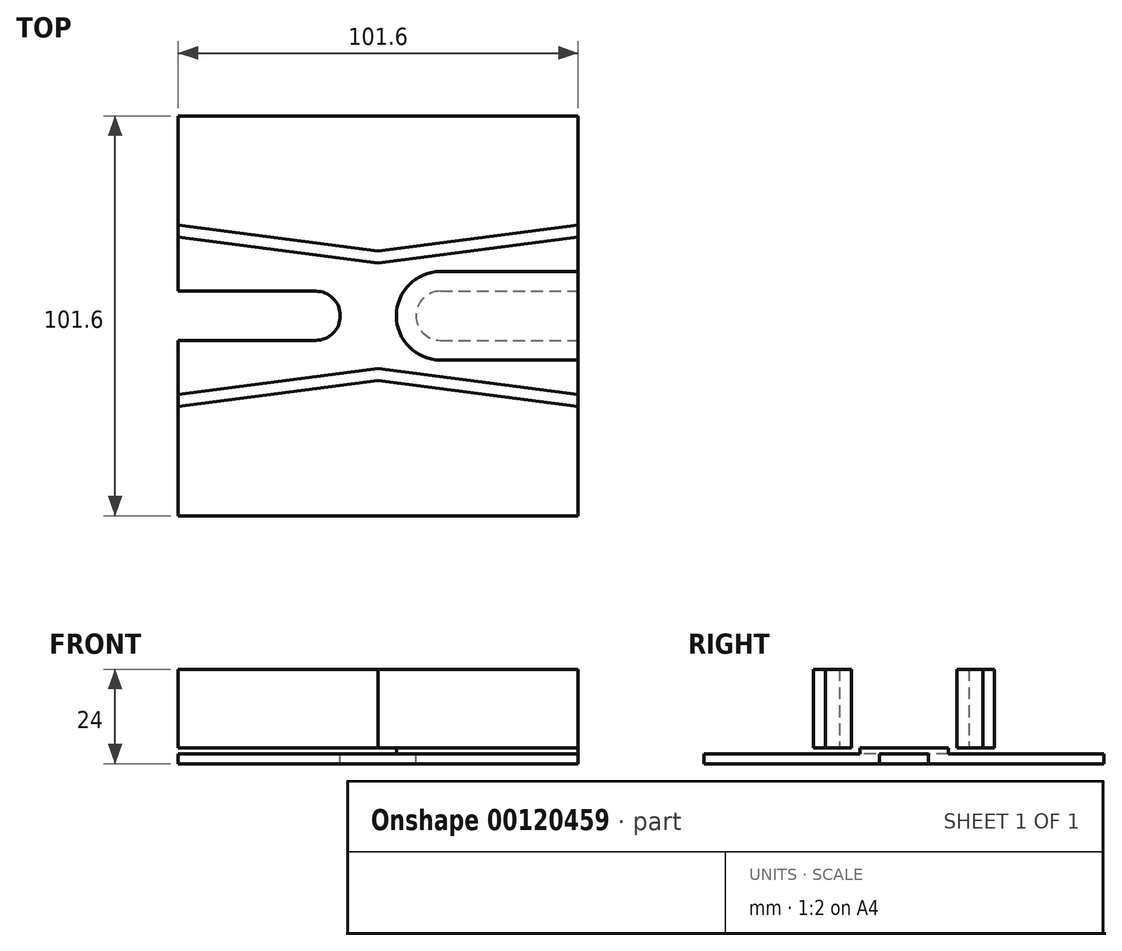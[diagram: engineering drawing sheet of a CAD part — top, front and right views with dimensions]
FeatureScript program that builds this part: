
annotation { "Feature Type Name" : "Feature", "Feature Type Description" : "" }
export const myFeature = defineFeature(function(context is Context, id is Id, definition is map)
    precondition{}
    {
        {
            var Q0;
            Q0=qCreatedBy(makeId("Top.planeOp"),FACE);
            var sketch = newSketch(context, id + "F0", { "sketchPlane" : qUnion([Q0])});
            skLineSegment(sketch, "E0.bottom", {"start": v(-50.8, -50.8) * mm, "end": v(50.8, -50.8) * mm});
            skLineSegment(sketch, "E0.top", {"start": v(-50.8, 50.8) * mm, "end": v(50.8, 50.8) * mm});
            skLineSegment(sketch, "E0.left", {"start": v(-50.8, -50.8) * mm, "end": v(-50.8, 50.8) * mm});
            skLineSegment(sketch, "E0.right", {"start": v(50.8, -50.8) * mm, "end": v(50.8, 50.8) * mm});
            skPoint(sketch, "E0.middle", {"position": v(0, 0) * mm});
            skSolve(sketch);
        }
        {
            var Q0;
            Q0=makeQuery(id+"F0.imprint","IMPRINT",FACE,{"disambiguationData":[TD([[makeQuery(id+"F0.imprint","IMPRINT",EDGE,{"derivedFrom":sQuery(id+"F0.wireOp",EDGE,"E0.bottom")}),1.0]])]});
            extrude(context, id + "F1", {"entities" : qUnion([Q0]), "depth" : 4 * mm});
        }
        {
            var Q0;
            Q0=makeQuery(id+"F1.opExtrude","CAP_FACE",FACE,{"disambiguationData":[OSD([sQuery(id+"F0.wireOp",EDGE,"E0.bottom"),sQuery(id+"F0.wireOp",EDGE,"E0.top"),sQuery(id+"F0.wireOp",EDGE,"E0.left"),sQuery(id+"F0.wireOp",EDGE,"E0.right")])],"isStart":false});
            var sketch = newSketch(context, id + "F2", { "sketchPlane" : qUnion([Q0])});
            skArc(sketch, "E1", {"start": v(-15.88, -11.25) * mm, "mid": v(-4.63, 0) * mm, "end": v(-15.87, 11.25) * mm});
            skLineSegment(sketch, "E2", {"start": v(0, 0) * mm, "end": v(0, 50.8) * mm, "construction": true});
            skArc(sketch, "E3.MirrorC", {"start": v(15.88, -11.25) * mm, "mid": v(4.63, 0) * mm, "end": v(15.87, 11.25) * mm});
            skLineSegment(sketch, "E4", {"start": v(-15.88, -11.25) * mm, "end": v(-50.8, -11.25) * mm});
            skLineSegment(sketch, "E5", {"start": v(0, 0) * mm, "end": v(-50.8, 0) * mm, "construction": true});
            skLineSegment(sketch, "E6.MirrorCS", {"start": v(-15.88, 11.25) * mm, "end": v(-50.8, 11.25) * mm});
            skLineSegment(sketch, "E7", {"start": v(-50.8, 11.25) * mm, "end": v(-50.8, -11.25) * mm});
            skLineSegment(sketch, "E8.MirrorCS", {"start": v(15.88, -11.25) * mm, "end": v(50.8, -11.25) * mm});
            skLineSegment(sketch, "E9.MirrorCS", {"start": v(15.88, 11.25) * mm, "end": v(50.8, 11.25) * mm});
            skLineSegment(sketch, "E10.MirrorCS", {"start": v(50.8, 11.25) * mm, "end": v(50.8, -11.25) * mm});
            skSolve(sketch);
        }
        {
            var Q0;
            Q0=makeQuery(id+"F2.imprint","IMPRINT",FACE,{"disambiguationData":[TD([[makeQuery(id+"F2.imprint","IMPRINT",EDGE,{"derivedFrom":sQuery(id+"F2.wireOp",EDGE,"E3.MirrorC")}),-1.0]])]});
            var Q1;
            Q1=makeQuery(id+"F2.imprint","IMPRINT",FACE,{"disambiguationData":[TD([[makeQuery(id+"F2.imprint","IMPRINT",EDGE,{"derivedFrom":sQuery(id+"F2.wireOp",EDGE,"E1")}),1.0]])]});
            extrude(context, id + "F3", {"entities" : qUnion([Q0, Q1]), "operationType" : NewBodyOperationType.REMOVE, "oppositeDirection" : true, "depth" : 1.5 * mm});
        }
        {
            var Q0;
            Q0=makeQuery(id+"F3.boolean.opBoolean","COPY",FACE,{"derivedFrom":makeQuery(id+"F3.opExtrude","CAP_FACE",FACE,{"disambiguationData":[OSD([sQuery(id+"F2.wireOp",EDGE,"E1"),sQuery(id+"F2.wireOp",EDGE,"E4"),sQuery(id+"F2.wireOp",EDGE,"E6.MirrorCS"),sQuery(id+"F2.wireOp",EDGE,"E7")])],"isStart":false})});
            var sketch = newSketch(context, id + "F4", { "sketchPlane" : qUnion([Q0])});
            skLineSegment(sketch, "E11.0", {"start": v(-15.88, 6.25) * mm, "end": v(-50.8, 6.25) * mm});
            skArc(sketch, "E11.1", {"start": v(-15.88, -6.25) * mm, "mid": v(-9.63, 0) * mm, "end": v(-15.88, 6.25) * mm});
            skLineSegment(sketch, "E11.2", {"start": v(-15.88, -6.25) * mm, "end": v(-50.8, -6.25) * mm});
            skLineSegment(sketch, "E12", {"start": v(-50.8, 6.25) * mm, "end": v(-50.8, -6.25) * mm});
            skLineSegment(sketch, "E13.MirrorCS", {"start": v(15.88, -6.25) * mm, "end": v(50.8, -6.25) * mm});
            skLineSegment(sketch, "E14.MirrorCS", {"start": v(15.88, 6.25) * mm, "end": v(50.8, 6.25) * mm});
            skArc(sketch, "E15.MirrorCS", {"start": v(15.88, -6.25) * mm, "mid": v(9.63, 0) * mm, "end": v(15.88, 6.25) * mm});
            skLineSegment(sketch, "E16.MirrorCS", {"start": v(50.8, 6.25) * mm, "end": v(50.8, -6.25) * mm});
            skSolve(sketch);
        }
        {
            var Q0;
            Q0=makeQuery(id+"F4.imprint","IMPRINT",FACE,{"disambiguationData":[TD([[makeQuery(id+"F4.imprint","IMPRINT",EDGE,{"derivedFrom":sQuery(id+"F4.wireOp",EDGE,"E11.0")}),1.0]])]});
            var Q1;
            Q1=makeQuery(id+"F4.imprint","IMPRINT",FACE,{"disambiguationData":[TD([[makeQuery(id+"F4.imprint","IMPRINT",EDGE,{"derivedFrom":sQuery(id+"F4.wireOp",EDGE,"E13.MirrorCS")}),1.0]])]});
            extrude(context, id + "F5", {"entities" : qUnion([Q0, Q1]), "operationType" : NewBodyOperationType.REMOVE, "oppositeDirection" : true, "depth" : 25.4 * mm});
        }
        {
            var Q0;
            Q0=makeQuery(id+"F1.opExtrude","CAP_FACE",FACE,{"disambiguationData":[OSD([sQuery(id+"F0.wireOp",EDGE,"E0.bottom"),sQuery(id+"F0.wireOp",EDGE,"E0.top"),sQuery(id+"F0.wireOp",EDGE,"E0.left"),sQuery(id+"F0.wireOp",EDGE,"E0.right")])],"isStart":false});
            var sketch = newSketch(context, id + "F6", { "sketchPlane" : qUnion([Q0])});
            skLineSegment(sketch, "E17", {"start": v(-50.8, 20) * mm, "end": v(0, 13.4) * mm});
            skLineSegment(sketch, "E18.MirrorCS", {"start": v(50.8, 20) * mm, "end": v(0, 13.4) * mm});
            skLineSegment(sketch, "E19.MirrorCS", {"start": v(-50.8, -20) * mm, "end": v(0, -13.4) * mm});
            skLineSegment(sketch, "E20.MirrorCS", {"start": v(50.8, -20) * mm, "end": v(0, -13.4) * mm});
            skLineSegment(sketch, "E21.0", {"start": v(50.8, 23.03) * mm, "end": v(0, 16.43) * mm});
            skLineSegment(sketch, "E21.1", {"start": v(-50.8, 23.03) * mm, "end": v(0, 16.43) * mm});
            skLineSegment(sketch, "E22", {"start": v(-50.8, 20) * mm, "end": v(-50.8, 23.03) * mm});
            skLineSegment(sketch, "E23.MirrorCS", {"start": v(50.8, 20) * mm, "end": v(50.8, 23.03) * mm});
            skPoint(sketch, "E24.orphan", {"position": v(-50.8, 31.03) * mm});
            skPoint(sketch, "E25.orphan", {"position": v(50.8, 31.03) * mm});
            skLineSegment(sketch, "E26.MirrorCS", {"start": v(-50.8, -23.03) * mm, "end": v(0, -16.43) * mm});
            skLineSegment(sketch, "E27.MirrorCS", {"start": v(50.8, -23.03) * mm, "end": v(0, -16.43) * mm});
            skLineSegment(sketch, "E28.MirrorCS", {"start": v(-50.8, -20) * mm, "end": v(-50.8, -23.03) * mm});
            skLineSegment(sketch, "E29.MirrorCS", {"start": v(50.8, -20) * mm, "end": v(50.8, -23.03) * mm});
            skSolve(sketch);
        }
        {
            var Q0;
            Q0=makeQuery(id+"F6.imprint","IMPRINT",FACE,{"disambiguationData":[TD([[makeQuery(id+"F6.imprint","IMPRINT",EDGE,{"derivedFrom":sQuery(id+"F6.wireOp",EDGE,"E19.MirrorCS")}),-1.0]])]});
            var Q1;
            Q1=makeQuery(id+"F6.imprint","IMPRINT",FACE,{"disambiguationData":[TD([[makeQuery(id+"F6.imprint","IMPRINT",EDGE,{"derivedFrom":sQuery(id+"F6.wireOp",EDGE,"E17")}),1.0]])]});
            extrude(context, id + "F7", {"entities" : qUnion([Q0, Q1]), "operationType" : NewBodyOperationType.ADD, "depth" : 20 * mm});
        }
    });
